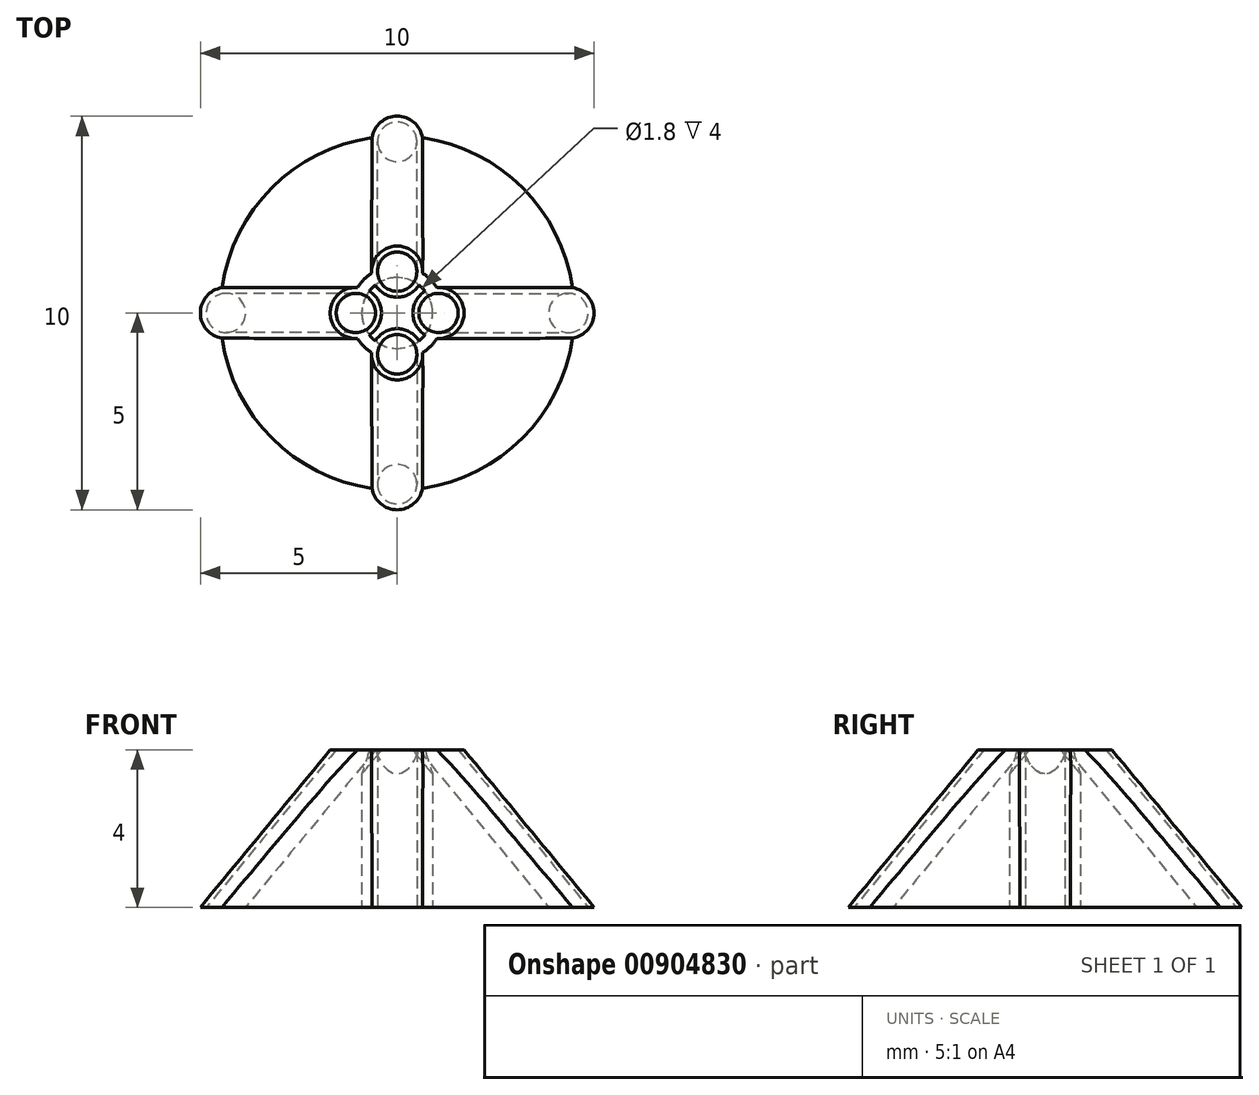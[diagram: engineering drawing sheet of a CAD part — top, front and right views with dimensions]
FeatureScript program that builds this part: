
annotation { "Feature Type Name" : "Feature", "Feature Type Description" : "" }
export const myFeature = defineFeature(function(context is Context, id is Id, definition is map)
    precondition{}
    {
        {
            var Q0;
            Q0=qCreatedBy(makeId("Front.planeOp"),FACE);
            var sketch = newSketch(context, id + "F0", { "sketchPlane" : qUnion([Q0])});
            skLineSegment(sketch, "E0", {"start": v(-0.9, 4) * mm, "end": v(-0.9, 0) * mm});
            skLineSegment(sketch, "E1", {"start": v(-0.9, 0) * mm, "end": v(-4.5, 0) * mm});
            skLineSegment(sketch, "E2", {"start": v(-0.9, 0) * mm, "end": v(0, 0) * mm, "construction": true});
            skLineSegment(sketch, "E3", {"start": v(0, 0) * mm, "end": v(0, 4) * mm, "construction": true});
            skLineSegment(sketch, "E4", {"start": v(0, 4) * mm, "end": v(-0.9, 4) * mm, "construction": true});
            skLineSegment(sketch, "E5", {"start": v(-0.9, 4) * mm, "end": v(-1.2, 4) * mm});
            skLineSegment(sketch, "E6", {"start": v(-1.2, 4) * mm, "end": v(-4.5, 0) * mm});
            skSolve(sketch);
        }
        {
            var Q0;
            Q0=makeQuery(id+"F0.imprint","IMPRINT",FACE,{"disambiguationData":[TD([[makeQuery(id+"F0.imprint","IMPRINT",EDGE,{"derivedFrom":sQuery(id+"F0.wireOp",EDGE,"E0")}),-1.0]])]});
            var Q1;
            Q1=sQuery(id+"F0.wireOp",EDGE,"E3");
            revolve(context, id + "F1", {"surfaceOperationType" : NewSurfaceOperationType.NEW, "entities" : qUnion([Q0]), "axis" : qUnion([Q1]), "revolveType" : RevolveType.FULL});
        }
        {
            var Q0;
            Q0=makeQuery(id+"F1.opRevolve","SWEPT_FACE",FACE,{"disambiguationData":[OSD([sQuery(id+"F0.wireOp",EDGE,"E5")])]});
            var sketch = newSketch(context, id + "F2", { "sketchPlane" : qUnion([Q0])});
            skLineSegment(sketch, "E7", {"start": v(0, 0.9) * mm, "end": v(0, 1.2) * mm, "construction": true});
            skCircle(sketch, "E8", {"center": v(0, 1.05) * mm, "radius": 0.65 * mm});
            skCircle(sketch, "E9", {"center": v(0, 1.05) * mm, "radius": 0.5 * mm});
            skSolve(sketch);
        }
        {
            var Q0;
            Q0=makeQuery(id+"F1.opRevolve","SWEPT_FACE",FACE,{"disambiguationData":[OSD([sQuery(id+"F0.wireOp",EDGE,"E6")])]});
            cPlane(context, id + "F3", {"entities" : qUnion([Q0]), "cplaneType" : CPlaneType.LINE_ANGLE, "offset" : 25 * mm, "angle" : 0 * degree, "width" : 150 * mm, "height" : 150 * mm});
        }
        {
            var Q0;
            Q0=qCreatedBy(id+"F3.planeOp",FACE);
            var sketch = newSketch(context, id + "F4", { "sketchPlane" : qUnion([Q0])});
            skLineSegment(sketch, "E10", {"start": v(1.2, 4) * mm, "end": v(4.5, 0) * mm});
            skLineSegment(sketch, "E11", {"start": v(-4.5, 0) * mm, "end": v(-1.2, 4) * mm});
            skPoint(sketch, "E12.0", {"position": v(-0.9, 4) * mm});
            skLineSegment(sketch, "E13", {"start": v(-0.9, 4) * mm, "end": v(-4.5, 0) * mm});
            skSolve(sketch);
        }
        {
            var Q0;
            {var subQ0=sQuery(id+"F2.wireOp",EDGE,"E8");var subQ1=makeQuery(id+"F1.opRevolve","SWEPT_EDGE",EDGE,{"disambiguationData":[OSD([sQuery(id+"F0.wireOp",EDGE,"E5"),sQuery(id+"F0.wireOp",EDGE,"E6")])]});var subQ2=makeQuery(id+"F2.imprint","INTERSECT",VERTEX,{"disambiguationData":[OD(0.0)],"derivedFrom":[subQ1,subQ0]});Q0=makeQuery(id+"F2.imprint","IMPRINT",FACE,{"disambiguationData":[TD([[makeQuery(id+"F2.imprint","IMPRINT",EDGE,{"disambiguationData":[TD([[subQ2,1.0]])],"derivedFrom":subQ0}),1.0]])]});}
            var Q1;
            {var subQ0=sQuery(id+"F2.wireOp",EDGE,"E8");var subQ1=sQuery(id+"F0.wireOp",EDGE,"E5");var subQ2=makeQuery(id+"F1.opRevolve","SWEPT_EDGE",EDGE,{"disambiguationData":[OSD([subQ1,sQuery(id+"F0.wireOp",EDGE,"E6")])]});var subQ3=makeQuery(id+"F2.imprint","INTERSECT",VERTEX,{"disambiguationData":[OD(0.0)],"derivedFrom":[subQ2,subQ0]});Q1=makeQuery(id+"F2.imprint","IMPRINT",FACE,{"disambiguationData":[TD([[makeQuery(id+"F2.imprint","IMPRINT",EDGE,{"disambiguationData":[TD([[subQ3,-1.0]])],"derivedFrom":subQ0}),1.0]])]});}
            var Q2;
            {var subQ0=sQuery(id+"F2.wireOp",EDGE,"E8");var subQ1=makeQuery(id+"F1.opRevolve","SWEPT_EDGE",EDGE,{"disambiguationData":[OSD([sQuery(id+"F0.wireOp",EDGE,"E0"),sQuery(id+"F0.wireOp",EDGE,"E5")])]});var subQ2=makeQuery(id+"F2.imprint","INTERSECT",VERTEX,{"disambiguationData":[OD(0.0)],"derivedFrom":[subQ1,subQ0]});Q2=makeQuery(id+"F2.imprint","IMPRINT",FACE,{"disambiguationData":[TD([[makeQuery(id+"F2.imprint","IMPRINT",EDGE,{"disambiguationData":[TD([[subQ2,-1.0]])],"derivedFrom":subQ0}),1.0]])]});}
            var Q3;
            {var subQ0=sQuery(id+"F2.wireOp",EDGE,"E8");var subQ1=sQuery(id+"F0.wireOp",EDGE,"E5");var subQ2=makeQuery(id+"F1.opRevolve","SWEPT_EDGE",EDGE,{"disambiguationData":[OSD([subQ1,sQuery(id+"F0.wireOp",EDGE,"E6")])]});var subQ3=makeQuery(id+"F2.imprint","INTERSECT",VERTEX,{"disambiguationData":[OD(1.0)],"derivedFrom":[subQ2,subQ0]});Q3=makeQuery(id+"F2.imprint","IMPRINT",FACE,{"disambiguationData":[TD([[makeQuery(id+"F2.imprint","IMPRINT",EDGE,{"disambiguationData":[TD([[subQ3,1.0]])],"derivedFrom":subQ0}),1.0]])]});}
            var Q4;
            Q4=sQuery(id+"F4.wireOp",EDGE,"E11");
            sweep(context, id + "F5", {"profiles" : qUnion([Q0, Q1, Q2, Q3]), "path" : qUnion([Q4])});
        }
        {
            var Q0;
            {var subQ0=sQuery(id+"F2.wireOp",EDGE,"E9");var subQ1=makeQuery(id+"F1.opRevolve","SWEPT_EDGE",EDGE,{"disambiguationData":[OSD([sQuery(id+"F0.wireOp",EDGE,"E5"),sQuery(id+"F0.wireOp",EDGE,"E6")])]});var subQ2=makeQuery(id+"F2.imprint","INTERSECT",VERTEX,{"disambiguationData":[OD(0.0)],"derivedFrom":[subQ1,subQ0]});Q0=makeQuery(id+"F2.imprint","IMPRINT",FACE,{"disambiguationData":[TD([[makeQuery(id+"F2.imprint","IMPRINT",EDGE,{"disambiguationData":[TD([[subQ2,1.0]])],"derivedFrom":subQ0}),1.0]])]});}
            var Q1;
            {var subQ0=sQuery(id+"F2.wireOp",EDGE,"E9");var subQ1=makeQuery(id+"F1.opRevolve","SWEPT_EDGE",EDGE,{"disambiguationData":[OSD([sQuery(id+"F0.wireOp",EDGE,"E0"),sQuery(id+"F0.wireOp",EDGE,"E5")])]});var subQ2=makeQuery(id+"F2.imprint","INTERSECT",VERTEX,{"disambiguationData":[OD(0.0)],"derivedFrom":[subQ1,subQ0]});Q1=makeQuery(id+"F2.imprint","IMPRINT",FACE,{"disambiguationData":[TD([[makeQuery(id+"F2.imprint","IMPRINT",EDGE,{"disambiguationData":[TD([[subQ2,-1.0]])],"derivedFrom":subQ0}),1.0]])]});}
            var Q2;
            {var subQ0=sQuery(id+"F2.wireOp",EDGE,"E9");var subQ1=sQuery(id+"F0.wireOp",EDGE,"E5");var subQ2=makeQuery(id+"F1.opRevolve","SWEPT_EDGE",EDGE,{"disambiguationData":[OSD([subQ1,sQuery(id+"F0.wireOp",EDGE,"E6")])]});var subQ3=makeQuery(id+"F2.imprint","INTERSECT",VERTEX,{"disambiguationData":[OD(0.0)],"derivedFrom":[subQ2,subQ0]});Q2=makeQuery(id+"F2.imprint","IMPRINT",FACE,{"disambiguationData":[TD([[makeQuery(id+"F2.imprint","IMPRINT",EDGE,{"disambiguationData":[TD([[subQ3,-1.0]])],"derivedFrom":subQ0}),1.0]])]});}
            var Q3;
            Q3=sQuery(id+"F4.wireOp",EDGE,"E11");
            sweep(context, id + "F6", {"operationType" : NewBodyOperationType.REMOVE, "profiles" : qUnion([Q0, Q1, Q2]), "path" : qUnion([Q3])});
        }
        {
            var Q0;
            Q0=makeQuery(id+"F5.opSweep","SWEPT_BODY",BODY,{"disambiguationData":[OSD([sQuery(id+"F2.wireOp",EDGE,"E8"),sQuery(id+"F2.wireOp",EDGE,"E9"),sQuery(id+"F4.wireOp",EDGE,"E11")])]});
            var Q1;
            Q1=makeQuery(id+"F6.boolean.opBoolean","COPY",FACE,{"derivedFrom":makeQuery(id+"F6.opSweep","SWEPT_FACE",FACE,{"disambiguationData":[OSD([sQuery(id+"F2.wireOp",EDGE,"E9"),sQuery(id+"F4.wireOp",EDGE,"E11")])]})});
            var Q2;
            Q2=makeQuery(id+"F1.opRevolve","SWEPT_FACE",FACE,{"disambiguationData":[OSD([sQuery(id+"F0.wireOp",EDGE,"E6")])]});
            circularPattern(context, id + "F7", {"patternType" : PatternType.FACE, "faces" : qUnion([Q1]), "axis" : qUnion([Q2]), "angle" : 360 * degree, "instanceCount" : 4, "equalSpace" : true});
        }
        {
            var Q0;
            Q0=makeQuery(id+"F5.opSweep","SWEPT_BODY",BODY,{"disambiguationData":[OSD([sQuery(id+"F2.wireOp",EDGE,"E8"),sQuery(id+"F2.wireOp",EDGE,"E9"),sQuery(id+"F4.wireOp",EDGE,"E11")])]});
            var Q1;
            Q1=makeQuery(id+"F1.opRevolve","SWEPT_FACE",FACE,{"disambiguationData":[OSD([sQuery(id+"F0.wireOp",EDGE,"E0")])]});
            circularPattern(context, id + "F8", {"entities" : qUnion([Q0]), "axis" : qUnion([Q1]), "angle" : 360 * degree, "instanceCount" : 4, "equalSpace" : true});
        }
        {
            var Q0;
            Q0=makeQuery(id+"F8.opPattern","COPY",BODY,{"derivedFrom":makeQuery(id+"F5.opSweep","SWEPT_BODY",BODY,{"disambiguationData":[OSD([sQuery(id+"F2.wireOp",EDGE,"E8"),sQuery(id+"F2.wireOp",EDGE,"E9"),sQuery(id+"F4.wireOp",EDGE,"E11")])]}),"instanceName":"2"});
            var Q1;
            Q1=makeQuery(id+"F8.opPattern","COPY",BODY,{"derivedFrom":makeQuery(id+"F5.opSweep","SWEPT_BODY",BODY,{"disambiguationData":[OSD([sQuery(id+"F2.wireOp",EDGE,"E8"),sQuery(id+"F2.wireOp",EDGE,"E9"),sQuery(id+"F4.wireOp",EDGE,"E11")])]}),"instanceName":"3"});
            var Q2;
            Q2=makeQuery(id+"F5.opSweep","SWEPT_BODY",BODY,{"disambiguationData":[OSD([sQuery(id+"F2.wireOp",EDGE,"E8"),sQuery(id+"F2.wireOp",EDGE,"E9"),sQuery(id+"F4.wireOp",EDGE,"E11")])]});
            var Q3;
            Q3=makeQuery(id+"F8.opPattern","COPY",BODY,{"derivedFrom":makeQuery(id+"F5.opSweep","SWEPT_BODY",BODY,{"disambiguationData":[OSD([sQuery(id+"F2.wireOp",EDGE,"E8"),sQuery(id+"F2.wireOp",EDGE,"E9"),sQuery(id+"F4.wireOp",EDGE,"E11")])]}),"instanceName":"1"});
            var Q4;
            Q4=makeQuery(id+"F1.opRevolve","SWEPT_BODY",BODY,{"disambiguationData":[OSD([sQuery(id+"F0.wireOp",EDGE,"E0"),sQuery(id+"F0.wireOp",EDGE,"E1"),sQuery(id+"F0.wireOp",EDGE,"E5"),sQuery(id+"F0.wireOp",EDGE,"E6")])]});
            booleanBodies(context, id + "F9", {"operationType" : BooleanOperationType.UNION, "tools" : qUnion([Q0, Q1, Q2, Q3, Q4])});
        }
    });
